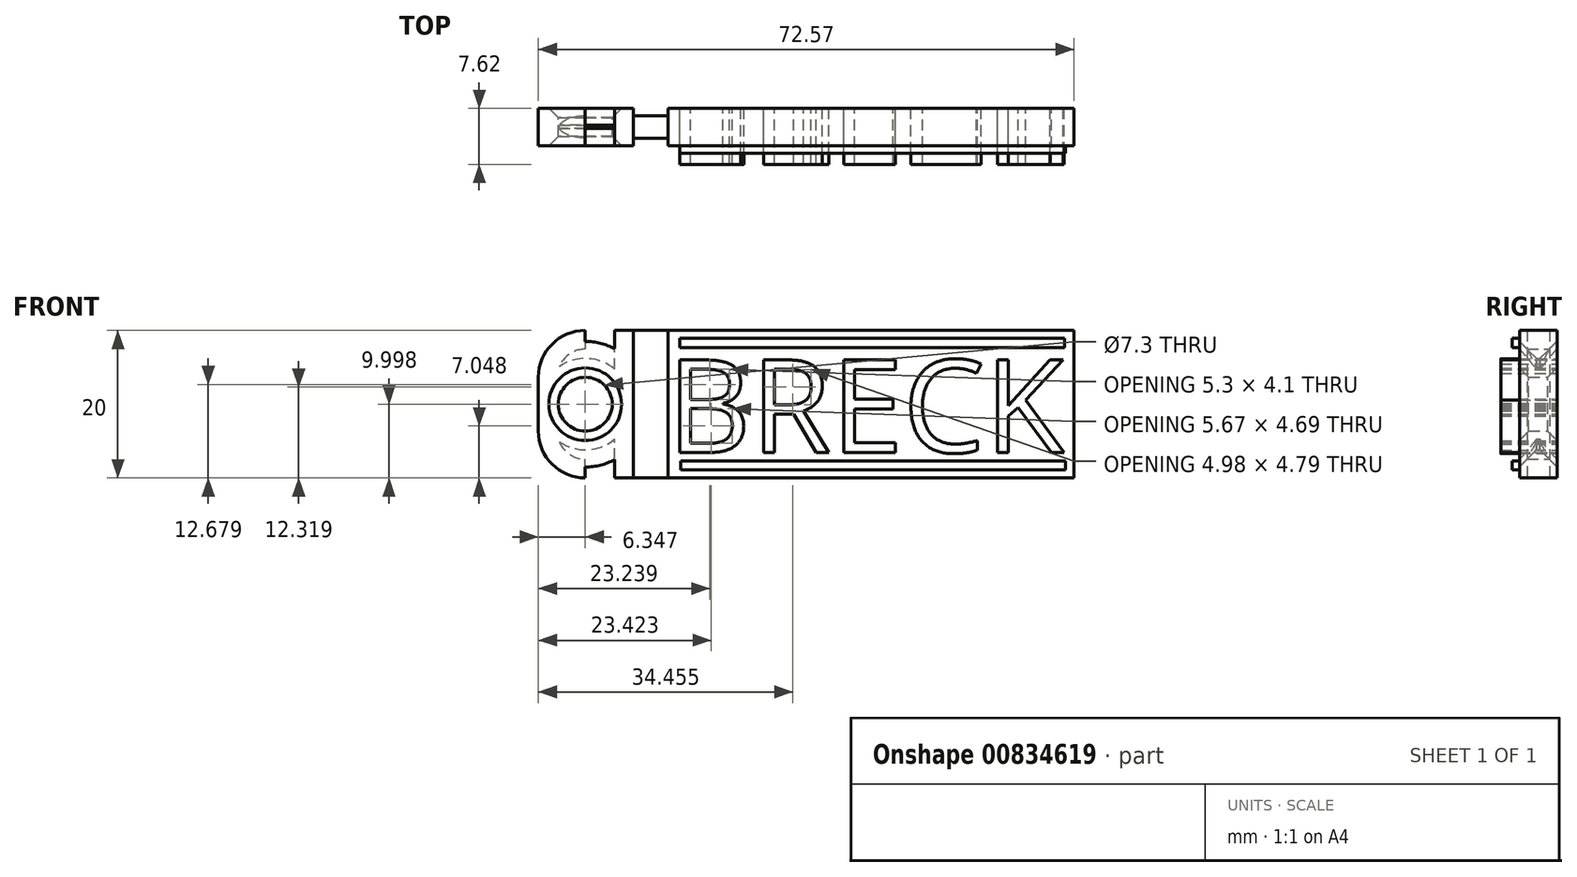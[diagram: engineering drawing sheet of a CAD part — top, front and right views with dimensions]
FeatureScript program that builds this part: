
annotation { "Feature Type Name" : "Feature", "Feature Type Description" : "" }
export const myFeature = defineFeature(function(context is Context, id is Id, definition is map)
    precondition{}
    {
        {
            var Q0;
            Q0=qCreatedBy(makeId("Front.planeOp"),FACE);
            var sketch = newSketch(context, id + "F0", { "sketchPlane" : qUnion([Q0])});
            skText(sketch, "E0", { "text": "BRECK", "fontName": "OpenSans-Regular.ttf"});
            const initialGuessF0  = {"E0": [-0.0275, 0.01255, 1, 0, 0.01264]};
            skSetInitialGuess(sketch, initialGuessF0);
            skSolve(sketch);
        }
        {
            var Q0;
            Q0 = qSketchRegion(id + "F0", true);
            var Q1;
            Q1=makeQuery(id+"F0.imprint","IMPRINT",FACE,{"disambiguationData":[TD([[makeQuery(id+"F0.imprint","IMPRINT",EDGE,{"derivedFrom":sQuery(id+"F0.wireOp",EDGE,"E0.sketch_text.stroke-25")}),-1.0]])]});
            var Q2;
            Q2=makeQuery(id+"F0.imprint","IMPRINT",FACE,{"disambiguationData":[TD([[makeQuery(id+"F0.imprint","IMPRINT",EDGE,{"derivedFrom":sQuery(id+"F0.wireOp",EDGE,"E0.sketch_text.stroke-36")}),1.0]])]});
            var Q3;
            Q3=makeQuery(id+"F0.imprint","IMPRINT",FACE,{"disambiguationData":[TD([[makeQuery(id+"F0.imprint","IMPRINT",EDGE,{"derivedFrom":sQuery(id+"F0.wireOp",EDGE,"E0.sketch_text.stroke-11")}),1.0]])]});
            var Q4;
            Q4=makeQuery(id+"F0.imprint","IMPRINT",FACE,{"disambiguationData":[TD([[makeQuery(id+"F0.imprint","IMPRINT",EDGE,{"derivedFrom":sQuery(id+"F0.wireOp",EDGE,"E0.sketch_text.stroke-18")}),1.0]])]});
            var Q5;
            Q5=makeQuery(id+"F0.imprint","IMPRINT",FACE,{"disambiguationData":[TD([[makeQuery(id+"F0.imprint","IMPRINT",EDGE,{"derivedFrom":sQuery(id+"F0.wireOp",EDGE,"E0.sketch_text.stroke-43")}),-1.0]])]});
            var Q6;
            Q6=makeQuery(id+"F0.imprint","IMPRINT",FACE,{"disambiguationData":[TD([[makeQuery(id+"F0.imprint","IMPRINT",EDGE,{"derivedFrom":sQuery(id+"F0.wireOp",EDGE,"E0.sketch_text.stroke-55")}),-1.0]])]});
            var Q7;
            Q7=makeQuery(id+"F0.imprint","IMPRINT",FACE,{"disambiguationData":[TD([[makeQuery(id+"F0.imprint","IMPRINT",EDGE,{"derivedFrom":sQuery(id+"F0.wireOp",EDGE,"E0.sketch_text.stroke-70")}),-1.0]])]});
            extrude(context, id + "F1", {"entities" : qUnion([Q0, Q1, Q2, Q3, Q4, Q5, Q6, Q7]), "depth" : 7.62 * mm, "offsetDistance" : 25.4 * mm});
        }
        {
            var Q0;
            Q0=makeQuery(id+"F0.imprint","IMPRINT",FACE,{"disambiguationData":[TD([[makeQuery(id+"F0.imprint","IMPRINT",EDGE,{"derivedFrom":sQuery(id+"F0.wireOp",EDGE,"E0.sketch_text.stroke-11")}),1.0]])]});
            extrude(context, id + "F2", {"entities" : qUnion([Q0]), "operationType" : NewBodyOperationType.REMOVE, "depth" : 24.9 * mm, "offsetDistance" : 25.4 * mm});
        }
        {
            var Q0;
            Q0=makeQuery(id+"F0.imprint","IMPRINT",FACE,{"disambiguationData":[TD([[makeQuery(id+"F0.imprint","IMPRINT",EDGE,{"derivedFrom":sQuery(id+"F0.wireOp",EDGE,"E0.sketch_text.stroke-18")}),1.0]])]});
            var Q1;
            Q1=makeQuery(id+"F0.imprint","IMPRINT",FACE,{"disambiguationData":[TD([[makeQuery(id+"F0.imprint","IMPRINT",EDGE,{"derivedFrom":sQuery(id+"F0.wireOp",EDGE,"E0.sketch_text.stroke-36")}),1.0]])]});
            extrude(context, id + "F3", {"entities" : qUnion([Q0, Q1]), "operationType" : NewBodyOperationType.REMOVE, "depth" : 18.03 * mm, "offsetDistance" : 25.4 * mm});
        }
        {
            var Q0;
            Q0=makeQuery(id+"F0.imprint","IMPRINT",FACE,{"disambiguationData":[TD([[makeQuery(id+"F0.imprint","IMPRINT",EDGE,{"derivedFrom":sQuery(id+"F0.wireOp",EDGE,"E0.sketch_text.stroke-18")}),1.0]])]});
            extrude(context, id + "F4", {"entities" : qUnion([Q0]), "operationType" : NewBodyOperationType.REMOVE, "depth" : 17.78 * mm, "offsetDistance" : 25.4 * mm});
        }
        {
            var Q0;
            Q0=qCreatedBy(makeId("Front.planeOp"),FACE);
            var sketch = newSketch(context, id + "F5", { "sketchPlane" : qUnion([Q0])});
            skLineSegment(sketch, "E1.bottom", {"start": v(-27.34, 29.09) * mm, "end": v(27.66, 29.09) * mm});
            skLineSegment(sketch, "E1.top", {"start": v(-27.34, 9.09) * mm, "end": v(27.66, 9.09) * mm});
            skLineSegment(sketch, "E1.left", {"start": v(-27.34, 29.09) * mm, "end": v(-27.34, 9.09) * mm});
            skLineSegment(sketch, "E1.right", {"start": v(27.66, 29.09) * mm, "end": v(27.66, 9.09) * mm});
            skLineSegment(sketch, "E2", {"start": v(-47.27, 35.45) * mm, "end": v(27.73, 35.45) * mm, "construction": true});
            skLineSegment(sketch, "E3", {"start": v(35.96, -20.91) * mm, "end": v(35.96, 29.09) * mm, "construction": true});
            skLineSegment(sketch, "E4", {"start": v(-27.34, 29.09) * mm, "end": v(-32.02, 29.09) * mm});
            skLineSegment(sketch, "E5", {"start": v(-32.02, 29.09) * mm, "end": v(-32.02, 9.09) * mm});
            skLineSegment(sketch, "E6", {"start": v(-32.02, 9.09) * mm, "end": v(-27.34, 9.09) * mm});
            skLineSegment(sketch, "E7", {"start": v(-32.02, 29.09) * mm, "end": v(-38.56, 29.09) * mm});
            skLineSegment(sketch, "E8", {"start": v(-32.02, 9.09) * mm, "end": v(-38.56, 9.09) * mm});
            skLineSegment(sketch, "E9", {"start": v(-44.91, 15.44) * mm, "end": v(-44.91, 22.74) * mm});
            skPoint(sketch, "E10.visualSharp", {"position": v(-44.91, 29.09) * mm});
            skArc(sketch, "E10.filletArc", {"start": v(-38.56, 29.09) * mm, "mid": v(-43.05, 27.23) * mm, "end": v(-44.91, 22.74) * mm});
            skPoint(sketch, "E11.visualSharp", {"position": v(-44.91, 9.09) * mm});
            skArc(sketch, "E11.filletArc", {"start": v(-44.91, 15.44) * mm, "mid": v(-43.05, 10.95) * mm, "end": v(-38.56, 9.09) * mm});
            skCircle(sketch, "E12", {"center": v(-38.56, 19.09) * mm, "radius": 3.65 * mm});
            skLineSegment(sketch, "E13.bottom", {"start": v(-25.64, 11.41) * mm, "end": v(26.5, 11.41) * mm});
            skLineSegment(sketch, "E13.top", {"start": v(-25.64, 10.15) * mm, "end": v(26.5, 10.15) * mm});
            skLineSegment(sketch, "E13.left", {"start": v(-25.64, 11.41) * mm, "end": v(-25.64, 10.15) * mm});
            skLineSegment(sketch, "E13.right", {"start": v(26.5, 11.41) * mm, "end": v(26.5, 10.15) * mm});
            skLineSegment(sketch, "E14.MirrorCS", {"start": v(-25.78, 26.77) * mm, "end": v(26.35, 26.77) * mm});
            skLineSegment(sketch, "E15.MirrorCS", {"start": v(-25.78, 28.02) * mm, "end": v(26.35, 28.02) * mm});
            skLineSegment(sketch, "E16", {"start": v(-25.78, 26.77) * mm, "end": v(-25.78, 28.02) * mm});
            skLineSegment(sketch, "E17", {"start": v(26.35, 26.77) * mm, "end": v(26.35, 28.02) * mm});
            skSolve(sketch);
        }
        {
            var Q0;
            Q0=makeQuery(id+"F5.imprint","IMPRINT",FACE,{"disambiguationData":[TD([[makeQuery(id+"F5.imprint","IMPRINT",EDGE,{"derivedFrom":sQuery(id+"F5.wireOp",EDGE,"E1.bottom")}),-1.0]])]});
            var Q1;
            Q1=makeQuery(id+"F5.imprint","IMPRINT",FACE,{"disambiguationData":[TD([[makeQuery(id+"F5.imprint","IMPRINT",EDGE,{"derivedFrom":sQuery(id+"F5.wireOp",EDGE,"E5")}),-1.0]])]});
            extrude(context, id + "F6", {"entities" : qUnion([Q0, Q1]), "depth" : 5.08 * mm, "offsetDistance" : 25.4 * mm});
        }
        {
            var Q0;
            Q0=makeQuery(id+"F5.imprint","IMPRINT",FACE,{"disambiguationData":[TD([[makeQuery(id+"F5.imprint","IMPRINT",EDGE,{"derivedFrom":sQuery(id+"F5.wireOp",EDGE,"E1.left")}),-1.0]])]});
            extrude(context, id + "F7", {"entities" : qUnion([Q0]), "depth" : 4.06 * mm, "offsetDistance" : 25.4 * mm});
        }
        {
            var Q0;
            Q0=makeQuery(id+"F7.opExtrude","CAP_FACE",FACE,{"disambiguationData":[OSD([sQuery(id+"F5.wireOp",EDGE,"E1.left"),sQuery(id+"F5.wireOp",EDGE,"E4"),sQuery(id+"F5.wireOp",EDGE,"E5"),sQuery(id+"F5.wireOp",EDGE,"E6")])],"isStart":true});
            extrude(context, id + "F8", {"entities" : qUnion([Q0]), "operationType" : NewBodyOperationType.REMOVE, "oppositeDirection" : true, "depth" : 1.02 * mm, "offsetDistance" : 25.4 * mm});
        }
        {
            var Q0;
            Q0=makeQuery(id+"F5.imprint","IMPRINT",FACE,{"disambiguationData":[TD([[makeQuery(id+"F5.imprint","IMPRINT",EDGE,{"derivedFrom":sQuery(id+"F5.wireOp",EDGE,"E13.bottom")}),-1.0]])]});
            var Q1;
            Q1=makeQuery(id+"F5.imprint","IMPRINT",FACE,{"disambiguationData":[TD([[makeQuery(id+"F5.imprint","IMPRINT",EDGE,{"derivedFrom":sQuery(id+"F5.wireOp",EDGE,"E14.MirrorCS")}),1.0]])]});
            extrude(context, id + "F9", {"entities" : qUnion([Q0, Q1]), "operationType" : NewBodyOperationType.ADD, "depth" : 6.1 * mm, "offsetDistance" : 25.4 * mm});
        }
        {
            var Q0;
            Q0=makeQuery(id+"F6.opExtrude","CAP_EDGE",EDGE,{"disambiguationData":[OSD([sQuery(id+"F5.wireOp",EDGE,"E12")])],"isStart":false});
            chamfer(context, id + "F10", {"entities" : qUnion([Q0]), "width" : 1.27 * mm, "tangentPropagation" : true});
        }
        {
            var Q0;
            Q0=makeQuery(id+"F6.opExtrude","CAP_EDGE",EDGE,{"disambiguationData":[OSD([sQuery(id+"F5.wireOp",EDGE,"E12")])],"isStart":true});
            chamfer(context, id + "F11", {"entities" : qUnion([Q0]), "width" : 1.27 * mm, "tangentPropagation" : true});
        }
        {
            var Q0;
            Q0=makeQuery(id+"F6.opExtrude","SWEPT_FACE",FACE,{"disambiguationData":[OSD([sQuery(id+"F5.wireOp",EDGE,"E7")])]});
            var Q1;
            Q1=makeQuery(id+"F6.opExtrude","SWEPT_FACE",FACE,{"disambiguationData":[OSD([sQuery(id+"F5.wireOp",EDGE,"E8")])]});
            var Q2;
            Q2=makeQuery(id+"F6.opExtrude","CAP_FACE",FACE,{"disambiguationData":[OSD([sQuery(id+"F5.wireOp",EDGE,"E5"),sQuery(id+"F5.wireOp",EDGE,"E7"),sQuery(id+"F5.wireOp",EDGE,"E8"),sQuery(id+"F5.wireOp",EDGE,"E9"),sQuery(id+"F5.wireOp",EDGE,"E10.filletArc"),sQuery(id+"F5.wireOp",EDGE,"E11.filletArc"),sQuery(id+"F5.wireOp",EDGE,"E12")])],"isStart":false});
            var Q3;
            Q3=makeQuery(id+"F6.opExtrude","CAP_FACE",FACE,{"disambiguationData":[OSD([sQuery(id+"F5.wireOp",EDGE,"E5"),sQuery(id+"F5.wireOp",EDGE,"E7"),sQuery(id+"F5.wireOp",EDGE,"E8"),sQuery(id+"F5.wireOp",EDGE,"E9"),sQuery(id+"F5.wireOp",EDGE,"E10.filletArc"),sQuery(id+"F5.wireOp",EDGE,"E11.filletArc"),sQuery(id+"F5.wireOp",EDGE,"E12")])],"isStart":true});
            shell(context, id + "F12", {"entities" : qUnion([Q0, Q1, Q2, Q3]), "thickness" : 2.54 * mm});
        }
    });
